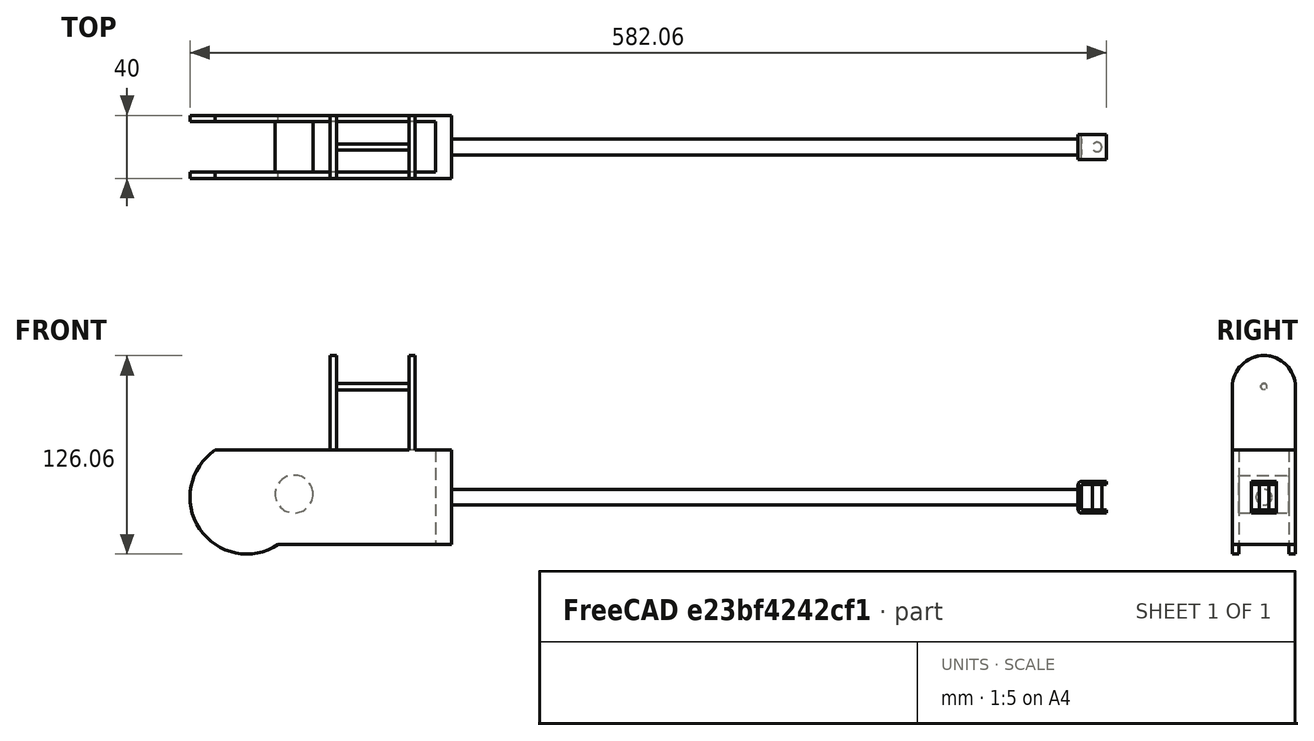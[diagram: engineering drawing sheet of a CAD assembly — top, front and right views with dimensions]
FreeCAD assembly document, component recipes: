
FREECAD ASSEMBLY — COMPONENT RECIPES ("ws1")

This assembly document has 4 components, labeled P0..P3 below (a component is one placed body or linked part). 2 of them carry a construction recipe — the FreeCAD feature program that regenerates the part from scratch, quoted from this document or its linked companion documents; the rest are supplied as boundary geometry only. No exploded tour is included for this assembly.
COMPONENT P0 — recipe-attached ("Body", modeled in this document).
Construction recipe (the document's own serialized feature program — sketch geometry with constraints, then the solid features built on it; lengths are millimeters unless a unit is written):

FEATURE [Sketcher::SketchObject] Sketch
  FullyConstrained = true
  MapMode = 5
  Placement = pos=(0,0,0) rot=(0.57735,0.57735,0.57735;2.0944rad)
  Support = -> [YZ_Plane]
  sketch-geometry (4):
    g0: LineSegment StartX=-20 StartY=0 StartZ=0 EndX=-20 EndY=40 EndZ=0
    g1: LineSegment StartX=-20 StartY=0 StartZ=0 EndX=20 EndY=0 EndZ=0
    g2: LineSegment StartX=20 StartY=0 StartZ=0 EndX=20 EndY=40 EndZ=0
    g3: ArcOfCircle CenterX=0 CenterY=40 CenterZ=0 NormalX=0 NormalY=0 NormalZ=1 AngleXU=0 Radius=20 StartAngle=-4.0634e-12 EndAngle=3.14159
  constraints (13):
    c: PointOnObject(g0,g-1)
    c: Vertical(g0)
    c: Coincident(g1,g0)
    c: PointOnObject(g1,g-1)
    c: Coincident(g2,g1)
    c: Vertical(g2)
    c: PointOnObject(g3,g-2)
    c: Coincident(g3,g0)
    c: Coincident(g2,g3)
    c: Equal(g0,g2)
    c: DistanceX(g0,g1) = 40
    c: DistanceY(g1,g2) = 40
    c: DistanceY(g-1,g3) = 40
FEATURE [PartDesign::Pad] Pad
  Direction = (1,-2e-16,3e-16)
  Length = 4
  Length2 = 10
  Midplane = true
  Placement = pos=(0,0,0) rot=(0.57735,0.57735,0.57735;2.0944rad)
  Profile = -> Sketch
  ReferenceAxis = -> Sketch [N_Axis]
  Type = 0
FEATURE [PartDesign::Body] Body
  Group = -> [Sketch,Pad]
  Origin = -> Origin
  Placement = pos=(25,0,0) rot=(0,0,1;0rad)
  Tip = -> Pad
COMPONENT P1 — recipe-attached ("Body001", modeled in this document).
Construction recipe (the document's own serialized feature program — sketch geometry with constraints, then the solid features built on it; lengths are millimeters unless a unit is written):

FEATURE [Sketcher::SketchObject] Sketch001
  FullyConstrained = true
  MapMode = 5
  Placement = pos=(0,0,0) rot=(1,0,0;1.5708rad)
  Support = -> [XZ_Plane001]
  sketch-geometry (4):
    g0: LineSegment StartX=50 StartY=-3.84723e-11 StartZ=0 EndX=-100 EndY=-3.84723e-11 EndZ=0
    g1: LineSegment StartX=50 StartY=-60 StartZ=0 EndX=-60 EndY=-60 EndZ=0
    g2: ArcOfCircle CenterX=-80 CenterY=-30 CenterZ=0 NormalX=0 NormalY=0 NormalZ=1 AngleXU=0 Radius=36.0555 StartAngle=2.1588 EndAngle=5.30039
    g3: LineSegment StartX=50 StartY=-3.84723e-11 StartZ=0 EndX=50 EndY=-60 EndZ=0
  constraints (13):
    c: PointOnObject(g0,g-1)
    c: Horizontal(g0)
    c: Horizontal(g1)
    c: Coincident(g2,g0)
    c: Coincident(g1,g2)
    c: Coincident(g3,g0)
    c: Coincident(g3,g1)
    c: Vertical(g3)
    c: DistanceX(g-1,g0) = 50
    c: DistanceX(g0,g-1) = 100
    c: DistanceY(g1,g0) = 60
    c: DistanceX(g1,g1) = 110
    c: DistanceX(g2,g1) = 20
FEATURE [PartDesign::Pad] Pad001  label="Pad002"
  Direction = (0,-1,2e-16)
  Length = 4
  Length2 = 10
  Placement = pos=(0,0,0) rot=(1,0,0;1.5708rad)
  Profile = -> Sketch001
  ReferenceAxis = -> Sketch001 [N_Axis]
  Reversed = true
  Type = 0
FEATURE [PartDesign::Body] Body001
  Group = -> [Sketch001,Pad001]
  Origin = -> Origin001
  Placement = pos=(0,-20,0) rot=(0,0,1;0rad)
  Tip = -> Pad001
COMPONENT P2 — geometry summary ("Pad001"; no construction recipe available for this part):
  bounding box: 60.0 x 40.0 x 4.0 mm
  tessellated surface: 260 triangles
  volume: 8913 mm^3 (93% of its bounding box)
  symmetry: 2-fold rotationally symmetric about the z axis; mirror-symmetric across its x mid-plane
COMPONENT P3 — geometry summary ("Pad003"; no construction recipe available for this part):
  bounding box: 166.1 x 66.1 x 4.0 mm
  tessellated surface: 260 triangles
  volume: 39368 mm^3 (90% of its bounding box)
  symmetry: mirror-symmetric across its y mid-plane
PROVENANCE & LICENSES
A FreeCAD (.FCStd) document from a public repository crawl; recipes are the document's own serialized feature recipes (and, for linked parts, companion documents' recipes).
License: as declared in the source repository (recorded in the dataset sidecar).
